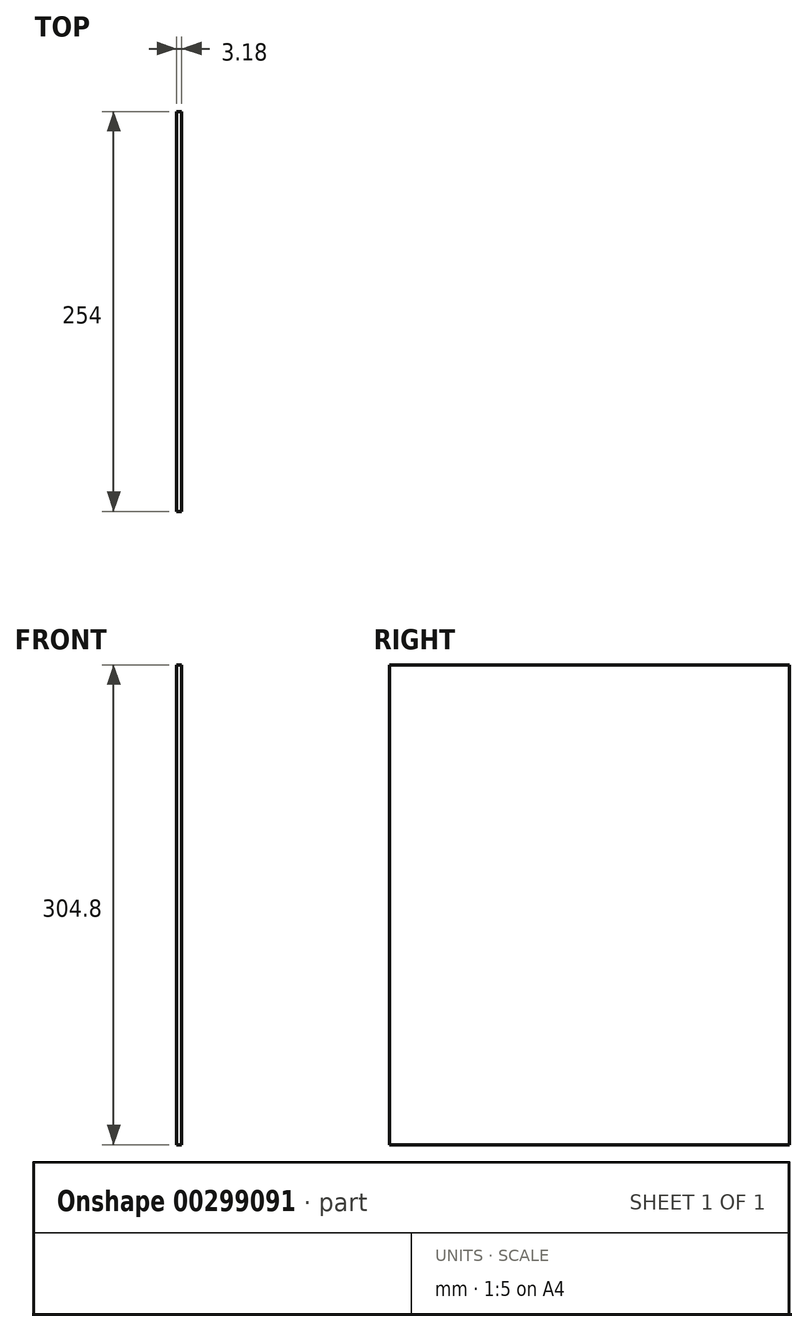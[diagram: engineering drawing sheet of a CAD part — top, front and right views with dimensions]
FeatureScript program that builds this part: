
annotation { "Feature Type Name" : "Feature", "Feature Type Description" : "" }
export const myFeature = defineFeature(function(context is Context, id is Id, definition is map)
    precondition{}
    {
        {
            var Q0;
            Q0=qCreatedBy(makeId("Right.planeOp"),FACE);
            var sketch = newSketch(context, id + "F0", { "sketchPlane" : qUnion([Q0])});
            skLineSegment(sketch, "E0.bottom", {"start": v(-127, 152.4) * mm, "end": v(127, 152.4) * mm});
            skLineSegment(sketch, "E0.top", {"start": v(-127, -152.4) * mm, "end": v(127, -152.4) * mm});
            skLineSegment(sketch, "E0.left", {"start": v(-127, 152.4) * mm, "end": v(-127, -152.4) * mm});
            skLineSegment(sketch, "E0.right", {"start": v(127, 152.4) * mm, "end": v(127, -152.4) * mm});
            skPoint(sketch, "E0.middle", {"position": v(0, 0) * mm});
            skSolve(sketch);
        }
        {
            var Q0;
            Q0 = qSketchRegion(id + "F0", true);
            extrude(context, id + "F1", {"entities" : qUnion([Q0]), "endBound" : BoundingType.SYMMETRIC, "depth" : 3.17 * mm});
        }
    });
